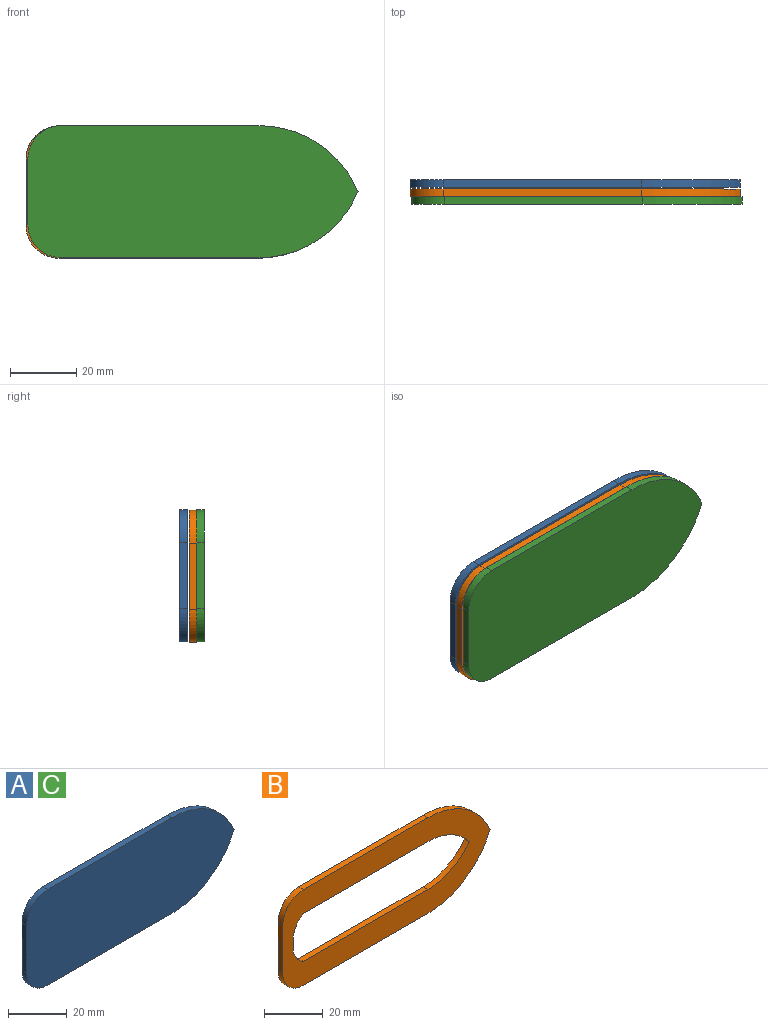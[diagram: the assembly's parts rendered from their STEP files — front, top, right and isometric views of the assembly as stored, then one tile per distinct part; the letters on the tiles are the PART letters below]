
ASSEMBLY  parts=3 mates=1
PART A: 9 faces, bbox 100x2.3x40 mm
  f0: plane 60x2.3mm, normal (0,0,1), area 138mm2, adj f1,f6,f7,f8
  f1: cylinder r=10mm len=10mm, axis (0,1,0), area 36.1mm2, adj f0,f2,f7,f8
  f2: plane 20x2.3mm, normal (-1,0,0), area 46mm2, adj f1,f3,f7,f8
  f3: cylinder r=10mm len=10mm, axis (0,1,0), area 36.1mm2, adj f2,f4,f7,f8
  f4: plane 60x2.3mm, normal (0,0,-1), area 138mm2, adj f3,f5,f7,f8
  f5: cylinder r=32.5mm len=30mm, axis (0,1,0), area 87.9mm2, adj f4,f6,f7,f8
  f6: cylinder r=32.5mm len=30mm, axis (0,1,0), area 87.9mm2, adj f0,f5,f7,f8
  f7: plane 100x40mm, normal (0,-1,0), area 3624.2mm2, adj f0,f1,f2,f3,f4,f5,f6
  f8: plane 100x40mm, normal (0,1,0), area 3624.2mm2, adj f0,f1,f2,f3,f4,f5,f6
PART B: 16 faces, bbox 100x2.3x40 mm
  f0: plane 60x2.3mm, normal (0,0,1), area 138mm2, adj f1,f6,f7,f8
  f1: cylinder r=10mm len=10mm, axis (0,1,0), area 36.1mm2, adj f0,f2,f7,f8
  f2: plane 20x2.3mm, normal (-1,0,0), area 46mm2, adj f1,f3,f7,f8
  f3: cylinder r=10mm len=10mm, axis (0,1,0), area 36.1mm2, adj f2,f4,f7,f8
  f4: plane 60x2.3mm, normal (0,0,-1), area 138mm2, adj f3,f5,f7,f8
  f5: cylinder r=32.5mm len=30mm, axis (0,1,0), area 87.9mm2, adj f4,f6,f7,f8
  f6: cylinder r=32.5mm len=30mm, axis (0,1,0), area 87.9mm2, adj f0,f5,f7,f8
  f7: plane 100x40mm, normal (0,-1,0), area 2069mm2, adj f0,f1,f2,f3,f4,f5,f6,f9
  f8: plane 100x40mm, normal (0,1,0), area 2069mm2, adj f0,f1,f2,f3,f4,f5,f6,f9
  f9: plane 60x2.3mm, normal (0,0,-1), area 138mm2, adj f7,f8,f10,f15
  f10: cylinder r=10mm len=7.42mm, axis (0,-1,0), area 21.3mm2, adj f7,f8,f9,f11
  f11: plane 5.17x2.3mm, normal (1,0,0), area 11.9mm2, adj f7,f8,f10,f12
  f12: cylinder r=10mm len=7.42mm, axis (0,-1,0), area 21.3mm2, adj f7,f8,f11,f13
  f13: plane 60x2.3mm, normal (0,0,1), area 138mm2, adj f7,f8,f12,f14
  f14: cylinder r=25mm len=20mm, axis (0,-1,0), area 53.3mm2, adj f7,f8,f13,f15
  f15: cylinder r=25mm len=20mm, axis (0,-1,0), area 53.3mm2, adj f7,f8,f9,f14
PART C: same geometry as A
PLACE A t=(9.56,-0.25,15.93)mm
PLACE B t=(-30.52,-3.06,-4.92)mm
PLACE C t=(10.11,-5.36,16)mm fixed
MATE planar C.f8 <-> B.f7  axis (0,1,0) through (-15.82,-5.36,15.28)mm
